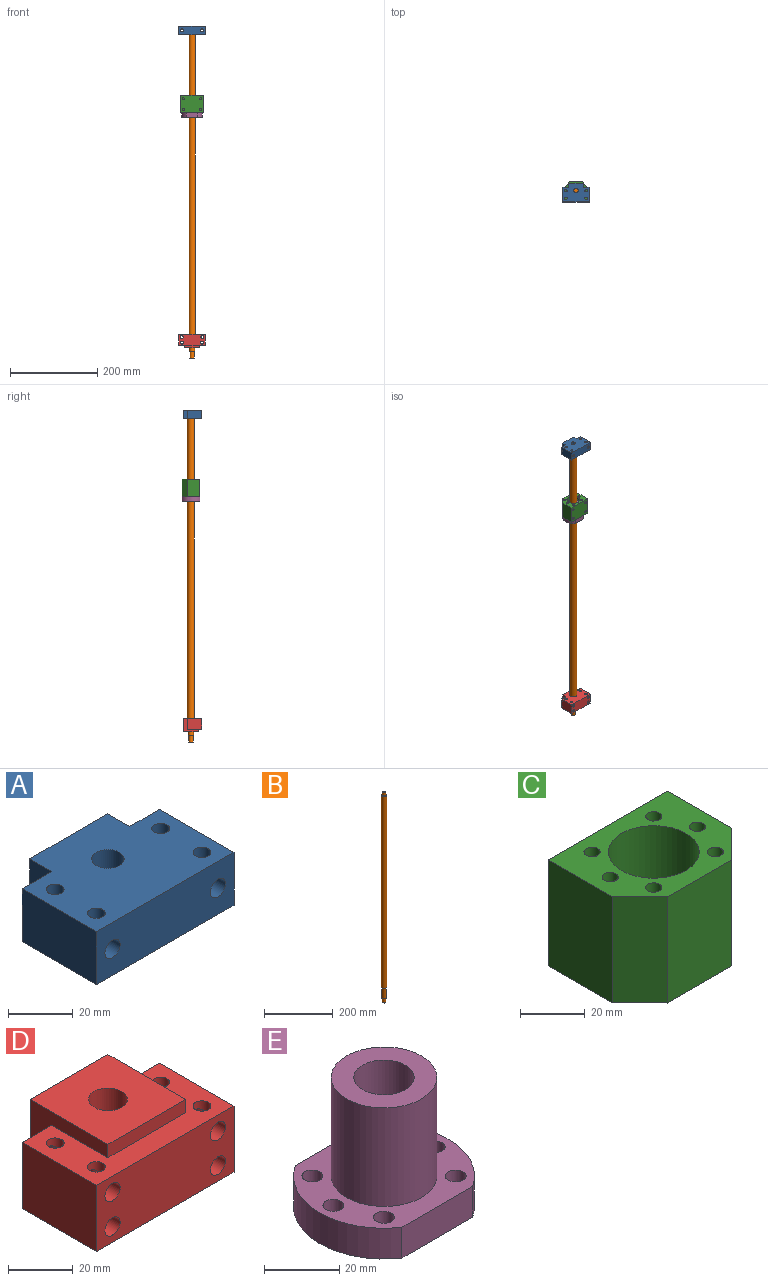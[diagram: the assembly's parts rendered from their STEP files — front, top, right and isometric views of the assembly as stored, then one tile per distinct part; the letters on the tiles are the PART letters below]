
ASSEMBLY  parts=5 mates=10
PART A: 25 faces, bbox 60x42.1x20 mm
  f0: cylinder r=3.3mm len=31mm, axis (0,1,0), area 535.9mm2, adj f2,f5,f8,f13,f18,f24
  f1: cylinder r=3.3mm len=31mm, axis (0,1,0), area 535.9mm2, adj f3,f4,f8,f14,f15,f22
  f2: cylinder r=2.75mm len=8.18mm, axis (0,0,-1), area 127.6mm2, adj f0,f19
  f3: cylinder r=2.75mm len=8.18mm, axis (0,0,-1), area 127.6mm2, adj f1,f19
  f4: cylinder r=2.75mm len=8.18mm, axis (0,0,-1), area 127.6mm2, adj f1,f19
  f5: cylinder r=2.75mm len=8.18mm, axis (0,0,-1), area 127.6mm2, adj f0,f19
  f6: plane 20x13mm, normal (0,1,0), area 168.4mm2, adj f7,f17,f19,f20,f23
  f7: plane 32.5x20mm, normal (-1,0,0), area 650mm2, adj f6,f8,f19,f20
  f8: plane 60x20mm, normal (0,-1,0), area 1131.6mm2, adj f0,f1,f7,f9,f19,f20
  f9: plane 32.5x20mm, normal (1,0,0), area 650mm2, adj f8,f10,f19,f20
  f10: plane 20x13mm, normal (0,1,0), area 168.4mm2, adj f9,f11,f19,f20,f21
  f11: plane 20x9.61mm, normal (1,0,0), area 192.2mm2, adj f10,f12,f19,f20
  f12: plane 34x20mm, normal (0,1,0), area 680mm2, adj f11,f17,f19,f20
  f13: cylinder r=2.75mm len=8.18mm, axis (0,0,-1), area 127.6mm2, adj f0,f20
  f14: cylinder r=2.75mm len=8.18mm, axis (0,0,-1), area 127.6mm2, adj f1,f20
  f15: cylinder r=2.75mm len=8.18mm, axis (0,0,-1), area 127.6mm2, adj f1,f20
  f16: cylinder r=5mm len=20mm, axis (0,0,-1), area 628.3mm2, adj f19,f20
  f17: plane 20x9.61mm, normal (-1,0,0), area 192.2mm2, adj f6,f12,f19,f20
  f18: cylinder r=2.75mm len=8.18mm, axis (0,0,-1), area 127.6mm2, adj f0,f20
  f19: plane 60x42.11mm, normal (0,0,1), area 2103.2mm2, adj f2,f3,f4,f5,f6,f7,f8,f9
  f20: plane 60x42.11mm, normal (0,0,-1), area 2103.2mm2, adj f6,f7,f8,f9,f10,f11,f12,f13
  f21: cylinder r=5.4mm len=10.8mm, axis (0,1,0), area 50.9mm2, adj f10,f22
  f22: plane 10.8x10.8mm, normal (0,1,0), area 57.4mm2, adj f1,f21
  f23: cylinder r=5.4mm len=10.8mm, axis (0,1,0), area 50.9mm2, adj f6,f24
  f24: plane 10.8x10.8mm, normal (0,1,0), area 57.4mm2, adj f0,f23
PART B: 9 faces, bbox 16x16x750 mm
  f0: cylinder r=5mm len=11mm, axis (0,0,-1), area 345.6mm2, adj f1,f2
  f1: plane 10x10mm, normal (0,0,1), area 78.5mm2, adj f0
  f2: plane 16x16mm, normal (0,0,1), area 122.5mm2, adj f0,f4
  f3: plane 16x16mm, normal (0,0,-1), area 88mm2, adj f4,f5
  f4: cylinder r=8mm len=685mm, axis (0,0,-1), area 34431.9mm2, adj f2,f3
  f5: cylinder r=6mm len=39mm, axis (0,0,-1), area 1470.3mm2, adj f3,f6
  f6: plane 12x12mm, normal (0,0,-1), area 34.6mm2, adj f5,f8
  f7: plane 10x10mm, normal (0,0,-1), area 78.5mm2, adj f8
  f8: cylinder r=5mm len=15mm, axis (0,0,-1), area 471.2mm2, adj f6,f7
PART C: 23 faces, bbox 52x40x40 mm
  f0: plane 52x40mm, normal (0,1,0), area 2001.5mm2, adj f1,f11,f13,f14,f15,f17,f19,f21
  f1: plane 40x28mm, normal (-1,0,0), area 1120mm2, adj f0,f2,f13,f14
  f2: plane 40x12mm, normal (-0.71,-0.71,0), area 678.8mm2, adj f1,f3,f13,f14
  f3: plane 40x28mm, normal (0,-1,0), area 1120mm2, adj f2,f4,f13,f14
  f4: plane 40x12mm, normal (0.71,-0.71,0), area 678.8mm2, adj f3,f11,f13,f14
  f5: cylinder r=2.5mm len=40mm, axis (0,0,-1), area 628.3mm2, adj f13,f14
  f6: cylinder r=2.5mm len=40mm, axis (0,0,-1), area 628.3mm2, adj f13,f14
  f7: cylinder r=2.5mm len=40mm, axis (0,0,-1), area 628.3mm2, adj f13,f14
  f8: cylinder r=2.5mm len=40mm, axis (0,0,-1), area 628.3mm2, adj f13,f14
  f9: cylinder r=2.5mm len=40mm, axis (0,0,-1), area 628.3mm2, adj f13,f14
  f10: cylinder r=14mm len=40mm, axis (0,0,-1), area 3518.6mm2, adj f13,f14
  f11: plane 40x28mm, normal (1,0,0), area 1120mm2, adj f0,f4,f13,f14
  f12: cylinder r=2.5mm len=40mm, axis (0,0,-1), area 628.3mm2, adj f13,f14
  f13: plane 52x40mm, normal (0,0,1), area 1202.4mm2, adj f0,f1,f2,f3,f4,f5,f6,f7
  f14: plane 52x40mm, normal (0,0,-1), area 1202.4mm2, adj f0,f1,f2,f3,f4,f5,f6,f7
  f15: cylinder r=2.5mm len=15mm, axis (0,1,0), area 235.6mm2, adj f0,f16
  f16: plane 5x5mm, normal (0,1,0), area 19.6mm2, adj f15
  f17: cylinder r=2.5mm len=15mm, axis (0,1,0), area 235.6mm2, adj f0,f18
  f18: plane 5x5mm, normal (0,1,0), area 19.6mm2, adj f17
  f19: cylinder r=2.5mm len=15mm, axis (0,1,0), area 235.6mm2, adj f0,f20
  f20: plane 5x5mm, normal (0,1,0), area 19.6mm2, adj f19
  f21: cylinder r=2.5mm len=15mm, axis (0,1,0), area 235.6mm2, adj f0,f22
  f22: plane 5x5mm, normal (0,1,0), area 19.6mm2, adj f21
PART D: 37 faces, bbox 60x42x30 mm
  f0: cylinder r=3.3mm len=31mm, axis (0,1,0), area 535.9mm2, adj f14,f17,f18,f25,f26,f36
  f1: cylinder r=3.3mm len=31mm, axis (0,1,0), area 535.9mm2, adj f6,f7,f14,f25,f26,f34
  f2: cylinder r=3.3mm len=31mm, axis (0,1,0), area 535.9mm2, adj f4,f5,f14,f27,f28,f32
  f3: cylinder r=3.3mm len=31mm, axis (0,1,0), area 535.9mm2, adj f14,f15,f16,f27,f28,f30
  f4: cylinder r=2.75mm len=5.5mm, axis (0,0,-1), area 58.5mm2, adj f2,f21
  f5: cylinder r=2.75mm len=5.5mm, axis (0,0,-1), area 58.5mm2, adj f2,f21
  f6: cylinder r=2.75mm len=5.5mm, axis (0,0,-1), area 58.5mm2, adj f1,f21
  f7: cylinder r=2.75mm len=5.5mm, axis (0,0,-1), area 58.5mm2, adj f1,f21
  f8: plane 25x13mm, normal (0,1,0), area 141.8mm2, adj f9,f19,f21,f22,f29,f31
  f9: plane 34x30mm, normal (1,0,0), area 407.5mm2, adj f8,f10,f21,f22,f23,f24
  f10: plane 34x30mm, normal (0,1,0), area 1020mm2, adj f9,f11,f22,f23
  f11: plane 34x30mm, normal (-1,0,0), area 407.5mm2, adj f10,f12,f21,f22,f23,f24
  f12: plane 25x13mm, normal (0,1,0), area 141.8mm2, adj f11,f13,f21,f22,f33,f35
  f13: plane 32.5x25mm, normal (-1,0,0), area 812.5mm2, adj f12,f14,f21,f22
  f14: plane 60x25mm, normal (0,-1,0), area 1363.2mm2, adj f0,f1,f2,f3,f13,f19,f21,f22
  f15: cylinder r=2.75mm len=5.5mm, axis (0,0,-1), area 58.5mm2, adj f3,f22
  f16: cylinder r=2.75mm len=5.5mm, axis (0,0,-1), area 58.5mm2, adj f3,f22
  f17: cylinder r=2.75mm len=5.5mm, axis (0,0,-1), area 58.5mm2, adj f0,f22
  f18: cylinder r=2.75mm len=5.5mm, axis (0,0,-1), area 58.5mm2, adj f0,f22
  f19: plane 32.5x25mm, normal (1,0,0), area 812.5mm2, adj f8,f14,f21,f22
  f20: cylinder r=6mm len=30mm, axis (0,0,-1), area 1131mm2, adj f22,f23
  f21: plane 60x32.5mm, normal (0,0,1), area 1022mm2, adj f4,f5,f6,f7,f8,f9,f11,f12
  f22: plane 60x42mm, normal (0,0,-1), area 2064.9mm2, adj f8,f9,f10,f11,f12,f13,f14,f15
  f23: plane 34x34mm, normal (0,0,1), area 1042.9mm2, adj f9,f10,f11,f20,f24
  f24: plane 34x5mm, normal (0,-1,0), area 170mm2, adj f9,f11,f21,f23
  f25: cylinder r=2.75mm len=9.35mm, axis (0,0,-1), area 134.2mm2, adj f0,f1
  f26: cylinder r=2.75mm len=9.35mm, axis (0,0,-1), area 134.2mm2, adj f0,f1
  f27: cylinder r=2.75mm len=9.35mm, axis (0,0,-1), area 134.2mm2, adj f2,f3
  f28: cylinder r=2.75mm len=9.35mm, axis (0,0,-1), area 134.2mm2, adj f2,f3
  f29: cylinder r=5.4mm len=10.8mm, axis (0,1,0), area 50.9mm2, adj f8,f30
  f30: plane 10.8x10.8mm, normal (0,1,0), area 57.4mm2, adj f3,f29
  f31: cylinder r=5.4mm len=10.8mm, axis (0,1,0), area 50.9mm2, adj f8,f32
  f32: plane 10.8x10.8mm, normal (0,1,0), area 57.4mm2, adj f2,f31
  f33: cylinder r=5.4mm len=10.8mm, axis (0,1,0), area 50.9mm2, adj f12,f34
  f34: plane 10.8x10.8mm, normal (0,1,0), area 57.4mm2, adj f1,f33
  f35: cylinder r=5.4mm len=10.8mm, axis (0,1,0), area 50.9mm2, adj f12,f36
  f36: plane 10.8x10.8mm, normal (0,1,0), area 57.4mm2, adj f0,f35
PART E: 15 faces, bbox 48x40x42 mm
  f0: plane 26.53x10mm, normal (0,1,0), area 265.3mm2, adj f1,f3,f11,f12
  f1: cylinder r=24mm len=40mm, axis (0,0,-1), area 472.9mm2, adj f0,f2,f11,f12
  f2: plane 26.53x10mm, normal (0,-1,0), area 265.3mm2, adj f1,f3,f11,f12
  f3: cylinder r=24mm len=40mm, axis (0,0,-1), area 472.9mm2, adj f0,f2,f11,f12
  f4: cylinder r=2.75mm len=10mm, axis (0,0,-1), area 172.8mm2, adj f11,f12
  f5: cylinder r=2.75mm len=10mm, axis (0,0,-1), area 172.8mm2, adj f11,f12
  f6: cylinder r=2.75mm len=10mm, axis (0,0,-1), area 172.8mm2, adj f11,f12
  f7: cylinder r=2.75mm len=10mm, axis (0,0,-1), area 172.8mm2, adj f11,f12
  f8: cylinder r=2.75mm len=10mm, axis (0,0,-1), area 172.8mm2, adj f11,f12
  f9: cylinder r=2.75mm len=10mm, axis (0,0,-1), area 172.8mm2, adj f11,f12
  f10: cylinder r=8mm len=42mm, axis (0,0,-1), area 2111.2mm2, adj f12,f14
  f11: plane 48x40mm, normal (0,0,1), area 907.2mm2, adj f0,f1,f2,f3,f4,f5,f6,f7
  f12: plane 48x40mm, normal (0,0,-1), area 1321.9mm2, adj f0,f1,f2,f3,f4,f5,f6,f7
  f13: cylinder r=14mm len=32mm, axis (0,0,-1), area 2814.9mm2, adj f11,f14
  f14: plane 28x28mm, normal (0,0,1), area 414.7mm2, adj f10,f13
PLACE A t=(-108.07,-149.73,1671.5)mm
PLACE B t=(-2.27,-0.45,932.5)mm
PLACE C rot(axis=(1,0,0),180deg) t=(-120.9,55.75,1533)mm
PLACE D rot(axis=(0,1,0),180deg) t=(-87.39,-145.6,986.5)mm
PLACE E t=(-19.88,74.23,1483)mm
MATE cylindrical D.f20 <-> B.f0  axis (0,0,1) through (-51.13,34.99,986.5)mm
MATE planar C.f13 <-> E.f1  axis (0,0,-1) through (-51.13,33.07,1493)mm
MATE cylindrical E.f5 <-> C.f7  axis (0,0,-1) through (-64.57,48.42,1488)mm
MATE planar D.f14 <-> A.f8  axis (0,-1,0) through (-51.13,9.99,974)mm
MATE cylindrical C.f10 <-> E.f1  axis (0,0,1) through (-51.13,34.99,1493)mm
MATE cylindrical A.f16 <-> B.f0  axis (0,0,-1) through (-51.13,34.99,1671.5)mm
MATE planar D.f22 <-> B.f0  axis (0,0,1) through (-51.13,29.05,986.5)mm
MATE cylindrical E.f1 <-> B.f0  axis (0,0,-1) through (-51.13,34.99,1504)mm
MATE planar A.f20 <-> B.f0  axis (0,0,-1) through (-51.13,29.19,1671.5)mm
MATE cylindrical E.f9 <-> C.f6  axis (0,0,-1) through (-37.7,48.42,1488)mm
